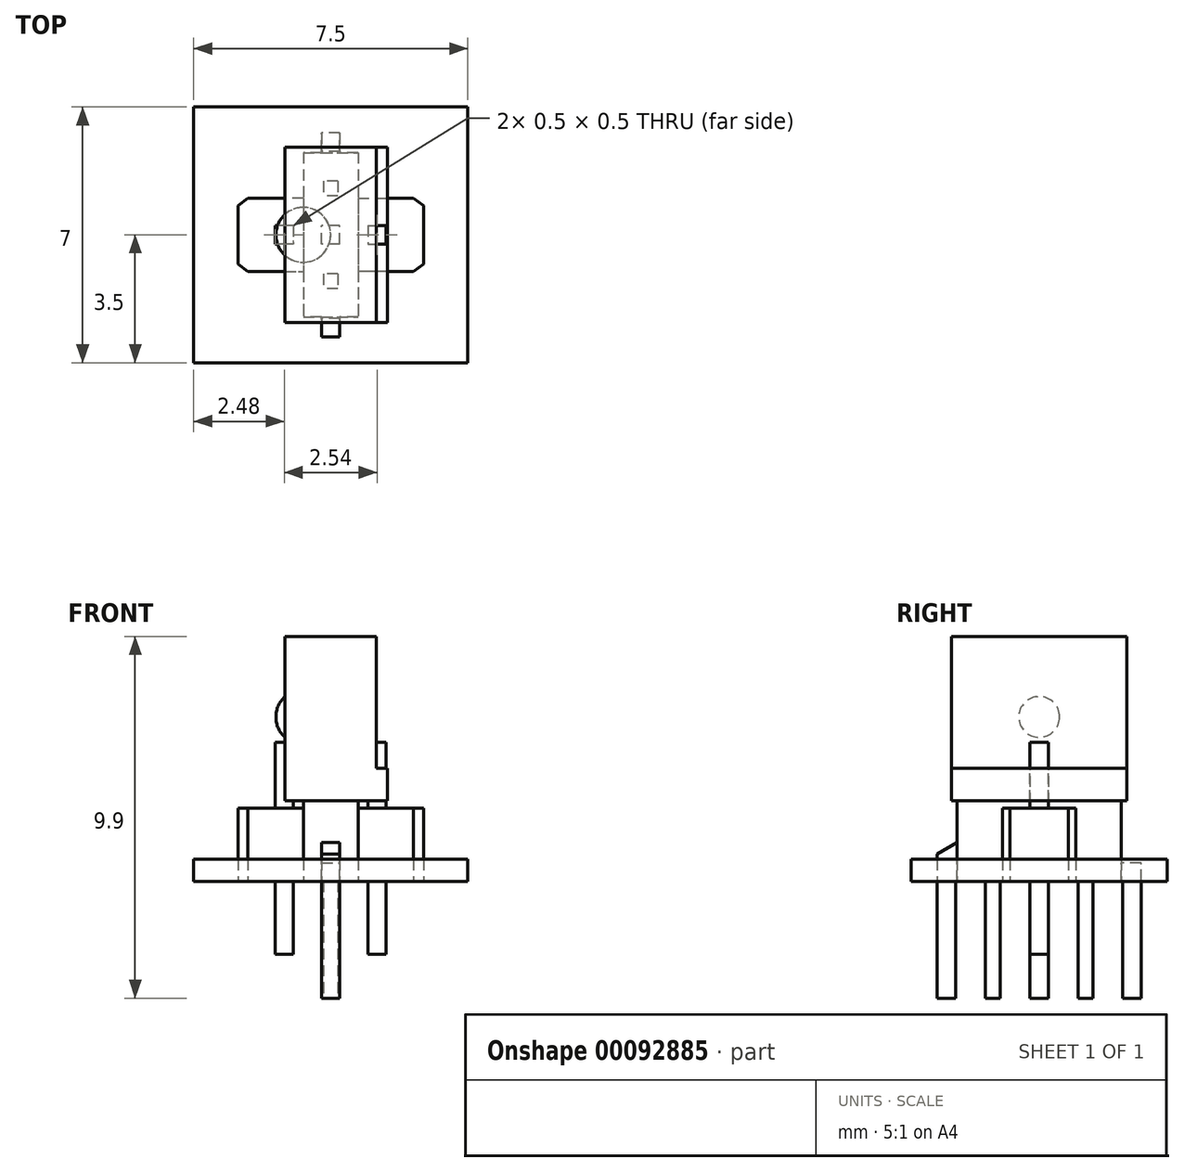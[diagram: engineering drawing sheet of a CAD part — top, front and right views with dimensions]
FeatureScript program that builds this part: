
annotation { "Feature Type Name" : "Feature", "Feature Type Description" : "" }
export const myFeature = defineFeature(function(context is Context, id is Id, definition is map)
    precondition{}
    {
        {
            var Q0;
            Q0=qCreatedBy(makeId("Top.planeOp"),FACE);
            cPlane(context, id + "F0", {"entities" : qUnion([Q0]), "cplaneType" : CPlaneType.OFFSET, "offset" : 2 * mm, "width" : 150 * mm, "height" : 150 * mm});
        }
        {
            var Q0;
            Q0=qCreatedBy(makeId("Front.planeOp"),FACE);
            var sketch = newSketch(context, id + "F1", { "sketchPlane" : qUnion([Q0])});
            skLineSegment(sketch, "E0", {"start": v(-1.25, 6.7) * mm, "end": v(1.25, 6.7) * mm});
            skLineSegment(sketch, "E1", {"start": v(1.25, 6.7) * mm, "end": v(1.25, 3.1) * mm});
            skLineSegment(sketch, "E2", {"start": v(1.25, 3.1) * mm, "end": v(1.55, 3.1) * mm});
            skLineSegment(sketch, "E3", {"start": v(1.55, 3.1) * mm, "end": v(1.55, 2.2) * mm});
            skLineSegment(sketch, "E4", {"start": v(1.55, 2.2) * mm, "end": v(-1.25, 2.2) * mm});
            skLineSegment(sketch, "E5", {"start": v(-1.25, 2.2) * mm, "end": v(-1.25, 6.7) * mm});
            skLineSegment(sketch, "E6", {"start": v(0, 8.99) * mm, "end": v(0, -1.06) * mm, "construction": true});
            skSolve(sketch);
        }
        {
            var Q0;
            Q0=qSketchRegion(id+"F1",true);
            extrude(context, id + "F2", {"entities" : qUnion([Q0]), "endBound" : BoundingType.SYMMETRIC, "depth" : 4.8 * mm});
        }
        {
            var Q0;
            Q0=qCreatedBy(makeId("Right.planeOp"),FACE);
            var sketch = newSketch(context, id + "F3", { "sketchPlane" : qUnion([Q0])});
            skLineSegment(sketch, "E7", {"start": v(0, 9.64) * mm, "end": v(0, -7.18) * mm, "construction": true});
            skLineSegment(sketch, "E8", {"start": v(2.54, 9.53) * mm, "end": v(2.54, -7.04) * mm, "construction": true});
            skLineSegment(sketch, "E9", {"start": v(-2.54, 9.6) * mm, "end": v(-2.54, -6.7) * mm, "construction": true});
            skLineSegment(sketch, "E10.bottom", {"start": v(0.25, 2.2) * mm, "end": v(-0.25, 2.2) * mm});
            skLineSegment(sketch, "E10.top", {"start": v(0.25, -3.2) * mm, "end": v(-0.25, -3.2) * mm});
            skLineSegment(sketch, "E10.left", {"start": v(0.25, 2.2) * mm, "end": v(0.25, -3.2) * mm});
            skLineSegment(sketch, "E10.right", {"start": v(-0.25, 2.2) * mm, "end": v(-0.25, -3.2) * mm});
            skLineSegment(sketch, "E11", {"start": v(1.25, 2.2) * mm, "end": v(1.25, 0) * mm});
            skLineSegment(sketch, "E12", {"start": v(1.25, 0) * mm, "end": v(2.3, 0) * mm});
            skLineSegment(sketch, "E13", {"start": v(2.3, 0) * mm, "end": v(2.3, -3.2) * mm});
            skLineSegment(sketch, "E14", {"start": v(2.3, -3.2) * mm, "end": v(2.8, -3.2) * mm});
            skLineSegment(sketch, "E15", {"start": v(2.8, -3.2) * mm, "end": v(2.8, 0.5) * mm});
            skLineSegment(sketch, "E16", {"start": v(2.8, 0.5) * mm, "end": v(1.75, 0.5) * mm});
            skLineSegment(sketch, "E17", {"start": v(1.75, 0.5) * mm, "end": v(1.75, 2.2) * mm});
            skLineSegment(sketch, "E18", {"start": v(1.75, 2.2) * mm, "end": v(1.25, 2.2) * mm});
            skLineSegment(sketch, "E19", {"start": v(-1.75, 2.2) * mm, "end": v(-1.75, 1.35) * mm});
            skLineSegment(sketch, "E20", {"start": v(-1.75, 1.35) * mm, "end": v(-2.8, 0.75) * mm});
            skLineSegment(sketch, "E21", {"start": v(-2.8, 0.75) * mm, "end": v(-2.8, -3.2) * mm});
            skLineSegment(sketch, "E22", {"start": v(-2.8, -3.2) * mm, "end": v(-2.3, -3.2) * mm});
            skLineSegment(sketch, "E23", {"start": v(-2.29, -3.2) * mm, "end": v(-2.3, 0) * mm});
            skLineSegment(sketch, "E24", {"start": v(-2.3, 0) * mm, "end": v(-1.25, 0) * mm});
            skLineSegment(sketch, "E25", {"start": v(-1.25, 0) * mm, "end": v(-1.25, 2.2) * mm});
            skLineSegment(sketch, "E26", {"start": v(-1.25, 2.2) * mm, "end": v(-1.75, 2.2) * mm});
            skLineSegment(sketch, "E27", {"start": v(4.1, 2.2) * mm, "end": v(-3.46, 2.2) * mm, "construction": true});
            skLineSegment(sketch, "E28", {"start": v(4.32, 0) * mm, "end": v(-4.48, 0) * mm, "construction": true});
            skLineSegment(sketch, "E29", {"start": v(4.16, -3.2) * mm, "end": v(-3.84, -3.2) * mm, "construction": true});
            skSolve(sketch);
        }
        {
            var Q0;
            Q0=qSketchRegion(id+"F3",true);
            extrude(context, id + "F4", {"entities" : qUnion([Q0]), "operationType" : NewBodyOperationType.ADD, "endBound" : BoundingType.SYMMETRIC, "depth" : 0.5 * mm});
        }
        {
            var Q0;
            Q0=qCreatedBy(makeId("Right.planeOp"),FACE);
            var sketch = newSketch(context, id + "F5", { "sketchPlane" : qUnion([Q0])});
            skLineSegment(sketch, "E30.bottom", {"start": v(2.25, 5.7) * mm, "end": v(-2.25, 5.7) * mm});
            skLineSegment(sketch, "E30.top", {"start": v(2.25, 0) * mm, "end": v(-2.25, 0) * mm});
            skLineSegment(sketch, "E30.left", {"start": v(2.25, 5.7) * mm, "end": v(2.25, 0) * mm});
            skLineSegment(sketch, "E30.right", {"start": v(-2.25, 5.7) * mm, "end": v(-2.25, 0) * mm});
            skLineSegment(sketch, "E31", {"start": v(0, 4.8) * mm, "end": v(0, -0.83) * mm, "construction": true});
            skSolve(sketch);
        }
        {
            var Q0;
            Q0=qSketchRegion(id+"F5",true);
            extrude(context, id + "F6", {"entities" : qUnion([Q0]), "endBound" : BoundingType.SYMMETRIC, "depth" : 1.5 * mm});
        }
        {
            var Q0;
            Q0=makeQuery(id+"F6.opExtrude","CAP_FACE",FACE,{"disambiguationData":[OSD([sQuery(id+"F5.wireOp",EDGE,"E30.bottom"),sQuery(id+"F5.wireOp",EDGE,"E30.top"),sQuery(id+"F5.wireOp",EDGE,"E30.left"),sQuery(id+"F5.wireOp",EDGE,"E30.right")])],"isStart":true});
            var sketch = newSketch(context, id + "F7", { "sketchPlane" : qUnion([Q0])});
            skArc(sketch, "E32", {"start": v(0, 5.25) * mm, "mid": v(-0.75, 4.5) * mm, "end": v(0, 3.75) * mm});
            skLineSegment(sketch, "E33", {"start": v(0, 5.25) * mm, "end": v(0, 3.75) * mm});
            skSolve(sketch);
        }
        {
            var Q0;
            Q0=qSketchRegion(id+"F7",true);
            var Q1;
            Q1=sQuery(id+"F7.wireOp",EDGE,"E33");
            revolve(context, id + "F8", {"operationType" : NewBodyOperationType.ADD, "entities" : qUnion([Q0]), "axis" : qUnion([Q1]), "revolveType" : RevolveType.FULL});
        }
        {
            var Q0;
            Q0=qCreatedBy(makeId("Right.planeOp"),FACE);
            var sketch = newSketch(context, id + "F9", { "sketchPlane" : qUnion([Q0])});
            skLineSegment(sketch, "E34", {"start": v(0, 7.5) * mm, "end": v(0, -5.02) * mm, "construction": true});
            skLineSegment(sketch, "E35", {"start": v(4.48, 0) * mm, "end": v(-4.1, 0) * mm, "construction": true});
            skLineSegment(sketch, "E36", {"start": v(-1.27, -3.2) * mm, "end": v(-1.27, 2.43) * mm, "construction": true});
            skLineSegment(sketch, "E37", {"start": v(1.27, 2.43) * mm, "end": v(1.27, -5.32) * mm, "construction": true});
            skLineSegment(sketch, "E38.bottom", {"start": v(1.47, 0) * mm, "end": v(1.07, 0) * mm});
            skLineSegment(sketch, "E38.top", {"start": v(1.47, -3.2) * mm, "end": v(1.07, -3.2) * mm});
            skLineSegment(sketch, "E38.left", {"start": v(1.47, 0) * mm, "end": v(1.47, -3.2) * mm});
            skLineSegment(sketch, "E38.right", {"start": v(1.07, 0) * mm, "end": v(1.07, -3.2) * mm});
            skLineSegment(sketch, "E39.bottom", {"start": v(-1.07, 0) * mm, "end": v(-1.47, 0) * mm});
            skLineSegment(sketch, "E39.top", {"start": v(-1.07, -3.2) * mm, "end": v(-1.47, -3.2) * mm});
            skLineSegment(sketch, "E39.left", {"start": v(-1.07, 0) * mm, "end": v(-1.07, -3.2) * mm});
            skLineSegment(sketch, "E39.right", {"start": v(-1.47, 0) * mm, "end": v(-1.47, -3.2) * mm});
            skSolve(sketch);
        }
        {
            var Q0;
            Q0=qSketchRegion(id+"F9",true);
            extrude(context, id + "F10", {"entities" : qUnion([Q0]), "operationType" : NewBodyOperationType.ADD, "endBound" : BoundingType.SYMMETRIC, "depth" : 0.4 * mm});
        }
        {
            var Q0;
            Q0=qCreatedBy(makeId("Top.planeOp"),FACE);
            var sketch = newSketch(context, id + "F11", { "sketchPlane" : qUnion([Q0])});
            skLineSegment(sketch, "E40", {"start": v(0, 0.8) * mm, "end": v(0.27, 1) * mm});
            skLineSegment(sketch, "E41", {"start": v(0.27, 1) * mm, "end": v(2.27, 1) * mm});
            skLineSegment(sketch, "E42", {"start": v(2.27, 1) * mm, "end": v(2.54, 0.8) * mm});
            skLineSegment(sketch, "E43", {"start": v(2.54, 0.8) * mm, "end": v(2.54, -0.8) * mm});
            skLineSegment(sketch, "E44", {"start": v(2.54, -0.8) * mm, "end": v(2.27, -1) * mm});
            skLineSegment(sketch, "E45", {"start": v(2.27, -1) * mm, "end": v(0.27, -1) * mm});
            skLineSegment(sketch, "E46", {"start": v(0.27, -1) * mm, "end": v(0, -0.8) * mm});
            skLineSegment(sketch, "E47", {"start": v(0, -0.8) * mm, "end": v(0, 0.8) * mm});
            skLineSegment(sketch, "E48", {"start": v(0, 2.31) * mm, "end": v(0, -1.41) * mm, "construction": true});
            skLineSegment(sketch, "E49", {"start": v(-0.3, 0) * mm, "end": v(0.1, 0) * mm, "construction": true});
            skLineSegment(sketch, "E50", {"start": v(1.27, 0.8) * mm, "end": v(1.27, -1.33) * mm, "construction": true});
            skLineSegment(sketch, "E51.bottom", {"start": v(1.02, 0.25) * mm, "end": v(1.52, 0.25) * mm});
            skLineSegment(sketch, "E51.top", {"start": v(1.02, -0.25) * mm, "end": v(1.52, -0.25) * mm});
            skLineSegment(sketch, "E51.left", {"start": v(1.02, 0.25) * mm, "end": v(1.02, -0.25) * mm});
            skLineSegment(sketch, "E51.right", {"start": v(1.52, 0.25) * mm, "end": v(1.52, -0.25) * mm});
            skLineSegment(sketch, "E52.0.MirrorCS", {"start": v(-0.27, 1) * mm, "end": v(-2.27, 1) * mm});
            skLineSegment(sketch, "E52.1.MirrorCS", {"start": v(-2.27, 1) * mm, "end": v(-2.54, 0.8) * mm});
            skLineSegment(sketch, "E52.2.MirrorCS", {"start": v(0, 0.8) * mm, "end": v(-0.27, 1) * mm});
            skLineSegment(sketch, "E52.3.MirrorCS", {"start": v(-1.02, 0.25) * mm, "end": v(-1.52, 0.25) * mm});
            skLineSegment(sketch, "E52.4.MirrorCS", {"start": v(-1.52, 0.25) * mm, "end": v(-1.52, -0.25) * mm});
            skLineSegment(sketch, "E52.5.MirrorCS", {"start": v(-1.02, 0.25) * mm, "end": v(-1.02, -0.25) * mm});
            skLineSegment(sketch, "E52.6.MirrorCS", {"start": v(-1.02, -0.25) * mm, "end": v(-1.52, -0.25) * mm});
            skLineSegment(sketch, "E52.7.MirrorCS", {"start": v(-2.54, 0.8) * mm, "end": v(-2.54, -0.8) * mm});
            skLineSegment(sketch, "E52.9.MirrorCS", {"start": v(-2.54, -0.8) * mm, "end": v(-2.27, -1) * mm});
            skLineSegment(sketch, "E52.10.MirrorCS", {"start": v(-2.27, -1) * mm, "end": v(-0.27, -1) * mm});
            skLineSegment(sketch, "E52.11.MirrorCS", {"start": v(-0.27, -1) * mm, "end": v(0, -0.8) * mm});
            skSolve(sketch);
        }
        {
            var Q0;
            Q0=qSketchRegion(id+"F11",true);
            extrude(context, id + "F12", {"entities" : qUnion([Q0]), "depth" : 2 * mm});
        }
        {
            var Q0;
            Q0=makeQuery(id+"F12.opExtrude","CAP_FACE",FACE,{"disambiguationData":[OSD([sQuery(id+"F11.wireOp",EDGE,"E40"),sQuery(id+"F11.wireOp",EDGE,"E41"),sQuery(id+"F11.wireOp",EDGE,"E42"),sQuery(id+"F11.wireOp",EDGE,"E43"),sQuery(id+"F11.wireOp",EDGE,"E44"),sQuery(id+"F11.wireOp",EDGE,"E45"),sQuery(id+"F11.wireOp",EDGE,"E46"),sQuery(id+"F11.wireOp",EDGE,"E51.bottom"),sQuery(id+"F11.wireOp",EDGE,"E51.top"),sQuery(id+"F11.wireOp",EDGE,"E51.left"),sQuery(id+"F11.wireOp",EDGE,"E51.right"),sQuery(id+"F11.wireOp",EDGE,"E52.0.MirrorCS"),sQuery(id+"F11.wireOp",EDGE,"E52.1.MirrorCS"),sQuery(id+"F11.wireOp",EDGE,"E52.2.MirrorCS"),sQuery(id+"F11.wireOp",EDGE,"E52.3.MirrorCS"),sQuery(id+"F11.wireOp",EDGE,"E52.4.MirrorCS"),sQuery(id+"F11.wireOp",EDGE,"E52.5.MirrorCS"),sQuery(id+"F11.wireOp",EDGE,"E52.6.MirrorCS"),sQuery(id+"F11.wireOp",EDGE,"E52.7.MirrorCS"),sQuery(id+"F11.wireOp",EDGE,"E52.9.MirrorCS"),sQuery(id+"F11.wireOp",EDGE,"E52.10.MirrorCS"),sQuery(id+"F11.wireOp",EDGE,"E52.11.MirrorCS")])],"isStart":false});
            var sketch = newSketch(context, id + "F13", { "sketchPlane" : qUnion([Q0])});
            skLineSegment(sketch, "E53.0", {"start": v(1.02, 0.25) * mm, "end": v(1.52, 0.25) * mm});
            skLineSegment(sketch, "E53.1", {"start": v(1.52, 0.25) * mm, "end": v(1.52, -0.25) * mm});
            skLineSegment(sketch, "E53.2", {"start": v(1.02, -0.25) * mm, "end": v(1.52, -0.25) * mm});
            skLineSegment(sketch, "E53.3", {"start": v(1.02, 0.25) * mm, "end": v(1.02, -0.25) * mm});
            skLineSegment(sketch, "E54.0", {"start": v(-1.02, 0.25) * mm, "end": v(-1.52, 0.25) * mm});
            skLineSegment(sketch, "E54.1", {"start": v(-1.02, 0.25) * mm, "end": v(-1.02, -0.25) * mm});
            skLineSegment(sketch, "E54.3", {"start": v(-1.52, 0.25) * mm, "end": v(-1.52, -0.25) * mm});
            skLineSegment(sketch, "E54.4", {"start": v(-1.02, -0.25) * mm, "end": v(-1.52, -0.25) * mm});
            skSolve(sketch);
        }
        {
            var Q0;
            Q0=qSketchRegion(id+"F13",true);
            extrude(context, id + "F14", {"entities" : qUnion([Q0]), "operationType" : NewBodyOperationType.ADD, "depth" : 1.8 * mm, "hasSecondDirection" : true, "secondDirectionOppositeDirection" : true, "secondDirectionDepth" : 4 * mm});
        }
        {
            var Q0;
            Q0=qCreatedBy(makeId("Top.planeOp"),FACE);
            var sketch = newSketch(context, id + "F15", { "sketchPlane" : qUnion([Q0])});
            skLineSegment(sketch, "E55.bottom", {"start": v(3.75, 3.5) * mm, "end": v(-3.75, 3.5) * mm});
            skLineSegment(sketch, "E55.top", {"start": v(3.75, -3.5) * mm, "end": v(-3.75, -3.5) * mm});
            skLineSegment(sketch, "E55.left", {"start": v(3.75, 3.5) * mm, "end": v(3.75, -3.5) * mm});
            skLineSegment(sketch, "E55.right", {"start": v(-3.75, 3.5) * mm, "end": v(-3.75, -3.5) * mm});
            skPoint(sketch, "E55.middle", {"position": v(0, 0) * mm});
            skSolve(sketch);
        }
        {
            var Q0;
            Q0=qSketchRegion(id+"F15",true);
            extrude(context, id + "F16", {"entities" : qUnion([Q0]), "depth" : 0.6 * mm});
        }
    });
